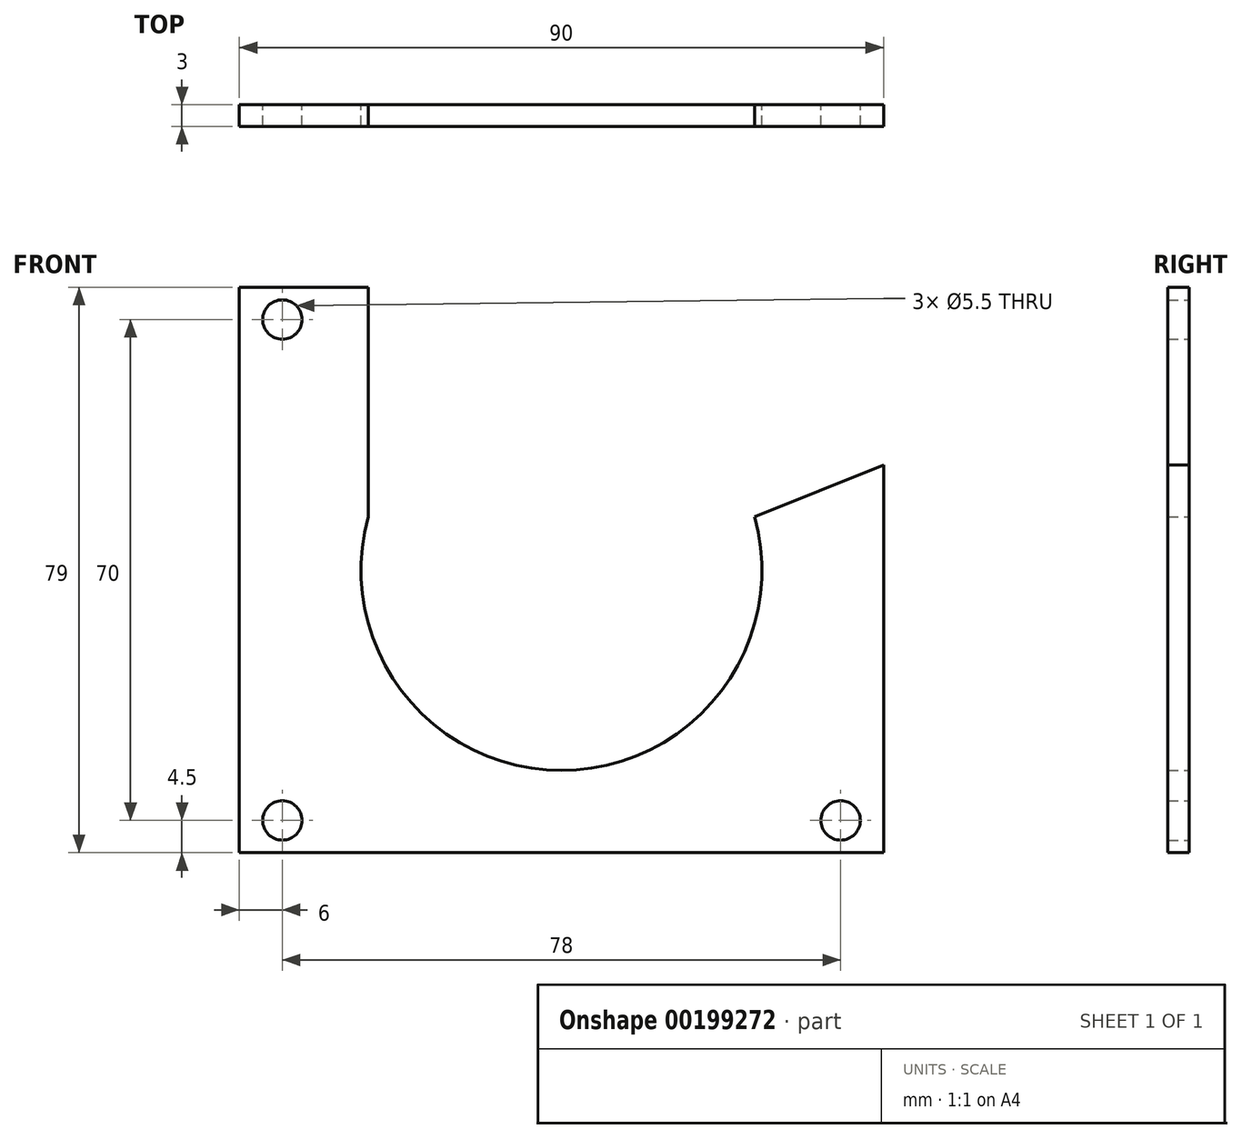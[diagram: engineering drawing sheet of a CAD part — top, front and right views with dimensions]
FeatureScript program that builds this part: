
annotation { "Feature Type Name" : "Feature", "Feature Type Description" : "" }
export const myFeature = defineFeature(function(context is Context, id is Id, definition is map)
    precondition{}
    {
        {
            var Q0;
            Q0=qCreatedBy(makeId("Front.planeOp"),FACE);
            var sketch = newSketch(context, id + "F0", { "sketchPlane" : qUnion([Q0])});
            skLineSegment(sketch, "E0.bottom", {"start": v(-45, 39.5) * mm, "end": v(-27, 39.5) * mm});
            skLineSegment(sketch, "E0.top", {"start": v(-45, -39.5) * mm, "end": v(45, -39.5) * mm});
            skLineSegment(sketch, "E0.left", {"start": v(-45, 39.5) * mm, "end": v(-45, -39.5) * mm});
            skLineSegment(sketch, "E0.right", {"start": v(45, 14.69) * mm, "end": v(45, -39.5) * mm});
            skPoint(sketch, "E0.middle", {"position": v(0, 0) * mm});
            skLineSegment(sketch, "E1", {"start": v(0, 39.5) * mm, "end": v(0, -39.5) * mm, "construction": true});
            skLineSegment(sketch, "E2", {"start": v(-45, 0) * mm, "end": v(45, 0) * mm, "construction": true});
            skCircle(sketch, "E3", {"center": v(-39, 35) * mm, "radius": 2.75 * mm});
            skCircle(sketch, "E4.MirrorC", {"center": v(-39, -35) * mm, "radius": 2.75 * mm});
            skCircle(sketch, "E5.MirrorC", {"center": v(39, -35) * mm, "radius": 2.75 * mm});
            skArc(sketch, "E6", {"start": v(-27, 7.42) * mm, "mid": v(0, -28) * mm, "end": v(27, 7.42) * mm});
            skLineSegment(sketch, "E7", {"start": v(-27, 39.5) * mm, "end": v(-27, 7.42) * mm});
            skLineSegment(sketch, "E8", {"start": v(-27, 7.42) * mm, "end": v(27, 7.42) * mm, "construction": true});
            skLineSegment(sketch, "E9", {"start": v(27, 7.42) * mm, "end": v(45, 14.69) * mm});
            skSolve(sketch);
        }
        {
            var Q0;
            Q0=qSketchRegion(id+"F0",true);
            extrude(context, id + "F1", {"entities" : qUnion([Q0]), "depth" : 3 * mm});
        }
    });
